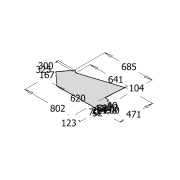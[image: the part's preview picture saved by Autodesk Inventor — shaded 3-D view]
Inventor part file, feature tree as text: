
AUTODESK INVENTOR PART (.ipt)
format: ipt  version: 2022 (Build 260153000, 153)  size: 109,568 bytes
history: native  units: mm
features: extrude x1, sketch x1
ambient origin geometry x8: Origin, YZ Plane, XZ Plane, XY Plane, X Axis, Y Axis, Z Axis, Center Point
bodies: Solid1 (feature_tree)
feature tree (2):
  extrude  "Extrusion1"  Depth=1.0mm
  sketch  "Sketch1"  dims[d0=620.0mm d1=802.0mm d2=167.0mm d3=685.0mm d4=325.0mm d5=641.0mm d6=300.0mm d7=104.0mm d8=471.0mm d9=123.0mm d10=200.0mm d11=70.0mm d12=198.0mm d13=173.0mm d14=22.0mm d15=143.0mm d16=40.0mm d17=80.0mm d18=52.0mm d19=42.0mm d20=1.0mm d21=0.0mm]
